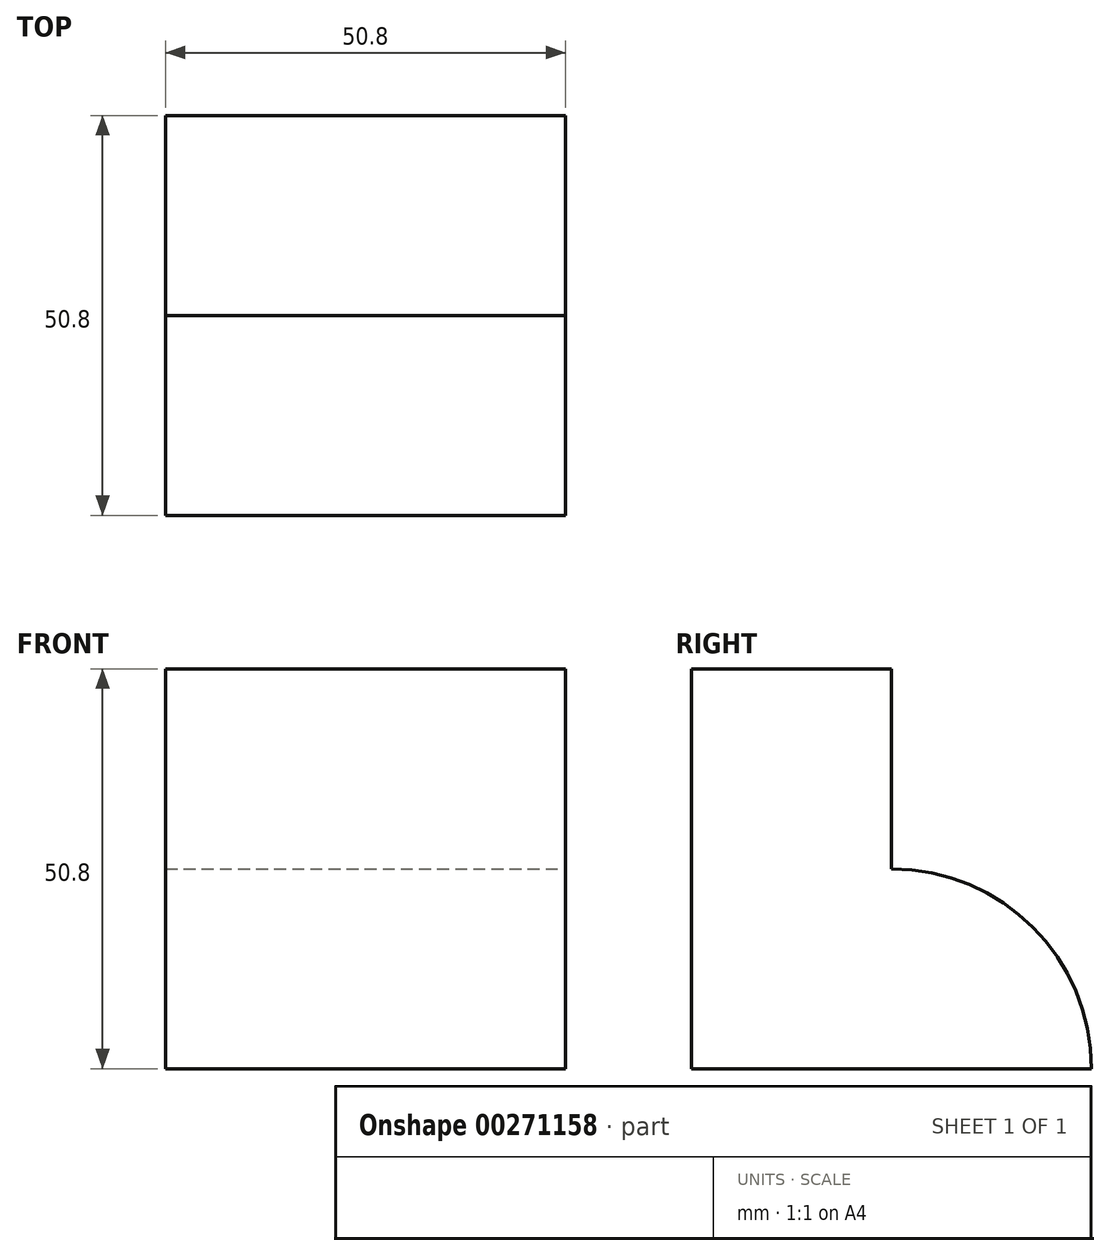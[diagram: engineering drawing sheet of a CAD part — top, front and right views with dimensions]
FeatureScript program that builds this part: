
annotation { "Feature Type Name" : "Feature", "Feature Type Description" : "" }
export const myFeature = defineFeature(function(context is Context, id is Id, definition is map)
    precondition{}
    {
        {
            var Q0;
            Q0=qCreatedBy(makeId("Front.planeOp"),FACE);
            var sketch = newSketch(context, id + "F0", { "sketchPlane" : qUnion([Q0])});
            skLineSegment(sketch, "E0", {"start": v(0, 0) * mm, "end": v(0, 50.8) * mm});
            skLineSegment(sketch, "E1", {"start": v(0, 50.8) * mm, "end": v(-50.8, 50.8) * mm});
            skLineSegment(sketch, "E2", {"start": v(-50.8, 50.8) * mm, "end": v(-50.8, 0) * mm});
            skLineSegment(sketch, "E3", {"start": v(-50.8, 0) * mm, "end": v(0, 0) * mm});
            skSolve(sketch);
        }
        {
            var Q0;
            Q0 = qSketchRegion(id + "F0", true);
            extrude(context, id + "F1", {"entities" : qUnion([Q0]), "depth" : 25.4 * mm});
        }
        {
            var Q0;
            Q0=qCreatedBy(makeId("Right.planeOp"),FACE);
            var sketch = newSketch(context, id + "F2", { "sketchPlane" : qUnion([Q0])});
            skLineSegment(sketch, "E4", {"start": v(0, 0) * mm, "end": v(25.4, 0) * mm});
            skLineSegment(sketch, "E5", {"start": v(0, 0) * mm, "end": v(0, 25.4) * mm});
            skArc(sketch, "E6", {"start": v(25.4, 0) * mm, "mid": v(17.96, 17.96) * mm, "end": v(0, 25.4) * mm});
            skSolve(sketch);
        }
        {
            var Q0;
            Q0 = qSketchRegion(id + "F2", true);
            extrude(context, id + "F3", {"entities" : qUnion([Q0]), "operationType" : NewBodyOperationType.ADD, "oppositeDirection" : true, "depth" : 50.8 * mm});
        }
    });
